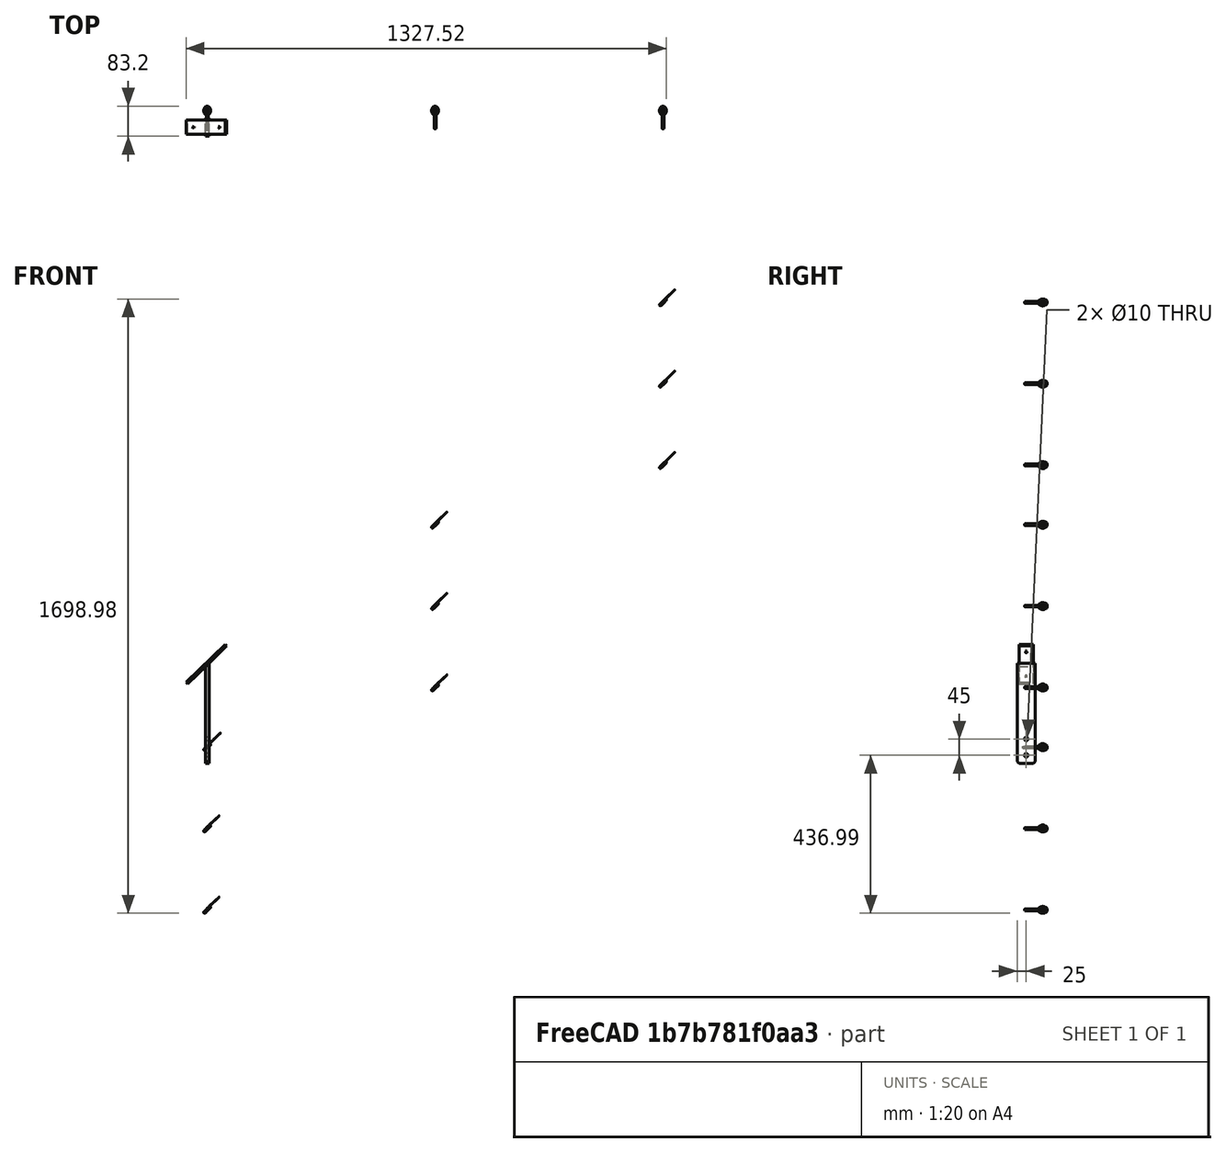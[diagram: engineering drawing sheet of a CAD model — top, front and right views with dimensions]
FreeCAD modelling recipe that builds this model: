
FCSTD DOCUMENT  (FreeCAD 0.17R10993 (Git))
Label: handrail_holder
License: All rights reserved
LicenseURL: http://en.wikipedia.org/wiki/All_rights_reserved
objects: Part::Part2DObjectPython×6, Part::Extrusion×6, Part::FeaturePython×3, Part::Compound×3, TechDraw::DrawProjGroupItem×3, Part::Cut×2, Part::Chamfer×1, App::DocumentObjectGroup×1, TechDraw::DrawSVGTemplate×1, TechDraw::DrawProjGroup×1, TechDraw::DrawViewPart×1, TechDraw::DrawPage×1
note: 21 computed .brp shape members not serialized (recipe doc carries the construction recipe); baked Part::Feature solids carry a one-line shape summary decoded from their .brp

FEATURE [Part::Part2DObjectPython] Circle  # Draft 2D object (typed FeaturePython)
  FirstAngle = 0
  LastAngle = 0
  MakeFace = true
  Placement = pos=(64.3902,-411,100) rot=(0.57735,-0.57735,-0.57735;2.0944rad)
  Radius = 5
FEATURE [Part::Extrusion] Extrude
  Base = -> Circle
  Dir = (1,0,0)
  DirMode = 0
  FaceMakerClass = Part::FaceMakerBullseye
  LengthFwd = 80
  LengthRev = 0
  Placement = pos=(25,0,0) rot=(0,0,1;0rad)
  Solid = false
  Symmetric = true
FEATURE [Part::FeaturePython] Array  # Draft array (typed FeaturePython)
  Angle = 360
  ArrayType = 0
  Axis = (0,0,1)
  Base = -> Extrude
  Center = (0,0,0)
  Fuse = false
  IntervalAxis = (0,0,0)
  IntervalX = (0,0,45)
  IntervalY = (0,0,225)
  IntervalZ = (0,0,0)
  NumberPolar = 1
  NumberX = 2
  NumberY = 5
  NumberZ = 1
  Placement = pos=(0,0,-27.5) rot=(0,0,1;0rad)
FEATURE [Part::Part2DObjectPython] Rectangle001  # Draft 2D object (typed FeaturePython)
  ChamferSize = 0
  Columns = 1
  FilletRadius = 0
  Height = 6
  Length = 150
  MakeFace = true
  Placement = pos=(35.7222,-9.99993,1170) rot=(0.866595,-0.352855,0.352855;1.71349rad)
  Rows = 1
FEATURE [Part::Part2DObjectPython] DWire001  # Draft 2D object (typed FeaturePython)
  ChamferSize = 0
  Closed = true
  End = (94.3902,-9.99993,1227.27)
  FilletRadius = 0
  Length = 568.751
  MakeFace = true
  Points = (4) [(84.3902,-9.99993,1217.51),(84.3902,-9.99995,950),(94.3902,-9.99995,950),(94.3902,-9.99993,1227.27)]
  Start = (84.3902,-9.99993,1217.51)
  Subdivisions = 0
FEATURE [Part::Extrusion] Extrude001
  Base = -> DWire001
  Dir = (0,1,0)
  DirMode = 0
  FaceMakerClass = Part::FaceMakerBullseye
  LengthFwd = 50
  LengthRev = 0
  Placement = pos=(0,-401,0) rot=(0,0,1;0rad)
  Solid = false
  Symmetric = true
FEATURE [Part::Extrusion] Extrude002
  Base = -> Rectangle001
  Dir = (0,1,0)
  DirMode = 0
  FaceMakerClass = Part::FaceMakerBullseye
  LengthFwd = 40
  LengthRev = 0
  Placement = pos=(0,-401,0) rot=(0,0,1;0rad)
  Solid = false
  Symmetric = true
FEATURE [Part::Part2DObjectPython] Circle001  # Draft 2D object (typed FeaturePython)
  FirstAngle = 0
  LastAngle = 0
  MakeFace = true
  Placement = pos=(125.169,-9.99992,1257.31) rot=(0.679504,0.679504,0.276676;2.60175rad)
  Radius = 2.5
FEATURE [Part::Part2DObjectPython] Circle002  # Draft 2D object (typed FeaturePython)
  FirstAngle = 0
  LastAngle = 0
  MakeFace = true
  Placement = pos=(53.6115,-9.99994,1187.46) rot=(0.679504,0.679504,0.276676;2.60175rad)
  Radius = 2.5
FEATURE [Part::Extrusion] Extrude003
  Base = -> Circle001
  Dir = (0.698537,8.477e-09,-0.715574)
  DirMode = 2
  FaceMakerClass = Part::FaceMakerBullseye
  LengthFwd = -10
  LengthRev = 0
  Solid = false
  Symmetric = false
FEATURE [Part::Extrusion] Extrude004
  Base = -> Circle002
  Dir = (0.698537,8.477e-09,-0.715574)
  DirMode = 2
  FaceMakerClass = Part::FaceMakerBullseye
  LengthFwd = -10
  LengthRev = 0
  Solid = false
  Symmetric = false
FEATURE [Part::Compound] Compound001
  Links = -> [Extrude003,Extrude004]
  Placement = pos=(0,-401,0) rot=(0,0,1;0rad)
FEATURE [Part::Cut] Cut001
  Base = -> Extrude002
  Tool = -> Compound001
FEATURE [Part::Chamfer] Chamfer002
  Base = -> Extrude001
  Edges = 2 edges r=5: [Edge6,Edge7]
FEATURE [Part::FeaturePython] railing_eyelet_01  # a2plus imported part (geometry in sourceFile) (typed FeaturePython)
  fixedPosition = true
  sourceFile = railing_eyelet.fcstd
  timeLastImport = 1.49443e+09
  updateColors = true
FEATURE [Part::Part2DObjectPython] Circle003  # Draft 2D object (typed FeaturePython)
  FirstAngle = 0
  LastAngle = 0
  MakeFace = true
  Placement = pos=(89.3902,-420.3,545) rot=(1,0,0;1.5708rad)
  Radius = 2.5
  Support = -> [railing_eyelet_01]
FEATURE [Part::Extrusion] Extrude006
  Base = -> Circle003
  Dir = (0,1,0)
  DirMode = 0
  FaceMakerClass = Part::FaceMakerBullseye
  LengthFwd = 35
  LengthRev = 0
  Solid = false
  Symmetric = false
FEATURE [Part::FeaturePython] Array006  # Draft array (typed FeaturePython)
  Angle = 360
  ArrayType = 0
  Axis = (0,0,1)
  Base = -> Extrude006
  Center = (0,0,0)
  Fuse = false
  IntervalAxis = (0,0,0)
  IntervalX = (0,0,225)
  IntervalY = (0,0,0)
  IntervalZ = (0,0,0)
  NumberPolar = 1
  NumberX = 3
  NumberY = 0
  NumberZ = 1
FEATURE [Part::Compound] Compound
  Links = -> [Array006,Array]
FEATURE [Part::Cut] Cut003
  Base = -> Chamfer002
  Tool = -> Compound
FEATURE [Part::Compound] Compound002  label="handrail_holder"
  Links = -> [Cut003,Cut001]
FEATURE [App::DocumentObjectGroup] Group  label="ref"
  Group = -> [railing_eyelet_01]
FEATURE [TechDraw::DrawSVGTemplate] Template
  Height = 841
  Orientation = 0
  Width = 594
FEATURE [TechDraw::DrawProjGroupItem] ProjItem  label="Front"
  ArcCenterMarks = true
  CenterScale = 2
  Direction = (0,-1,0)
  HardHidden = true
  HiddenWidth = 0.15
  HorizCenterLine = false
  IsoCount = 0
  IsoHidden = false
  IsoVisible = false
  IsoWidth = 0.3
  KeepLabel = false
  LineWidth = 0.7
  Rotation = 0
  RotationVector = (1,0,0)
  Scale = 0.5
  ScaleType = 2
  SeamHidden = false
  SeamVisible = false
  ShowSectionLine = true
  SmoothHidden = false
  SmoothVisible = false
  Source = -> Compound002
  Type = 0
  VertCenterLine = false
  X = 59.1919
  Y = -49.7877
FEATURE [TechDraw::DrawProjGroupItem] ProjItem001  label="Left"
  ArcCenterMarks = true
  CenterScale = 2
  Direction = (-1,0,0)
  HardHidden = true
  HiddenWidth = 0.15
  HorizCenterLine = false
  IsoCount = 0
  IsoHidden = false
  IsoVisible = false
  IsoWidth = 0.3
  KeepLabel = false
  LineWidth = 0.7
  Rotation = 0
  RotationVector = (0,1,0)
  Scale = 0.5
  ScaleType = 2
  SeamHidden = false
  SeamVisible = false
  ShowSectionLine = true
  SmoothHidden = false
  SmoothVisible = false
  Source = -> Compound002
  Type = 1
  VertCenterLine = false
  X = 80.7637
  Y = 0
FEATURE [TechDraw::DrawProjGroupItem] ProjItem002  label="Top"
  ArcCenterMarks = true
  CenterScale = 2
  Direction = (0,0,1)
  HardHidden = true
  HiddenWidth = 0.15
  HorizCenterLine = false
  IsoCount = 0
  IsoHidden = false
  IsoVisible = false
  IsoWidth = 0.3
  KeepLabel = false
  LineWidth = 0.7
  Rotation = 0
  RotationVector = (1,0,0)
  Scale = 0.5
  ScaleType = 2
  SeamHidden = false
  SeamVisible = false
  ShowSectionLine = true
  SmoothHidden = false
  SmoothVisible = false
  Source = -> Compound002
  Type = 4
  VertCenterLine = false
  X = 0
  Y = -139.536
FEATURE [TechDraw::DrawProjGroup] ProjGroup
  Anchor = -> ProjItem
  AutoDistribute = true
  KeepLabel = false
  ProjectionType = 0
  Rotation = 0
  Scale = 0.5
  ScaleType = 2
  Source = -> Compound002
  Views = -> [ProjItem,ProjItem001,ProjItem002]
  X = 297
  Y = 420.5
  spacingX = 25
  spacingY = -25
FEATURE [TechDraw::DrawViewPart] View
  ArcCenterMarks = true
  CenterScale = 2
  Direction = (-0.45,-1,0.5)
  HardHidden = true
  HiddenWidth = 0.15
  HorizCenterLine = false
  IsoCount = 0
  IsoHidden = false
  IsoVisible = false
  IsoWidth = 0.3
  KeepLabel = false
  LineWidth = 0.7
  Rotation = 0
  Scale = 0.5
  ScaleType = 2
  SeamHidden = false
  SeamVisible = false
  ShowSectionLine = true
  SmoothHidden = false
  SmoothVisible = false
  Source = -> Compound002
  VertCenterLine = false
  X = 456.073
  Y = 389.939
FEATURE [TechDraw::DrawPage] Page
  ProjectionType = 0
  Template = -> Template
  Views = -> [ProjGroup,View]
